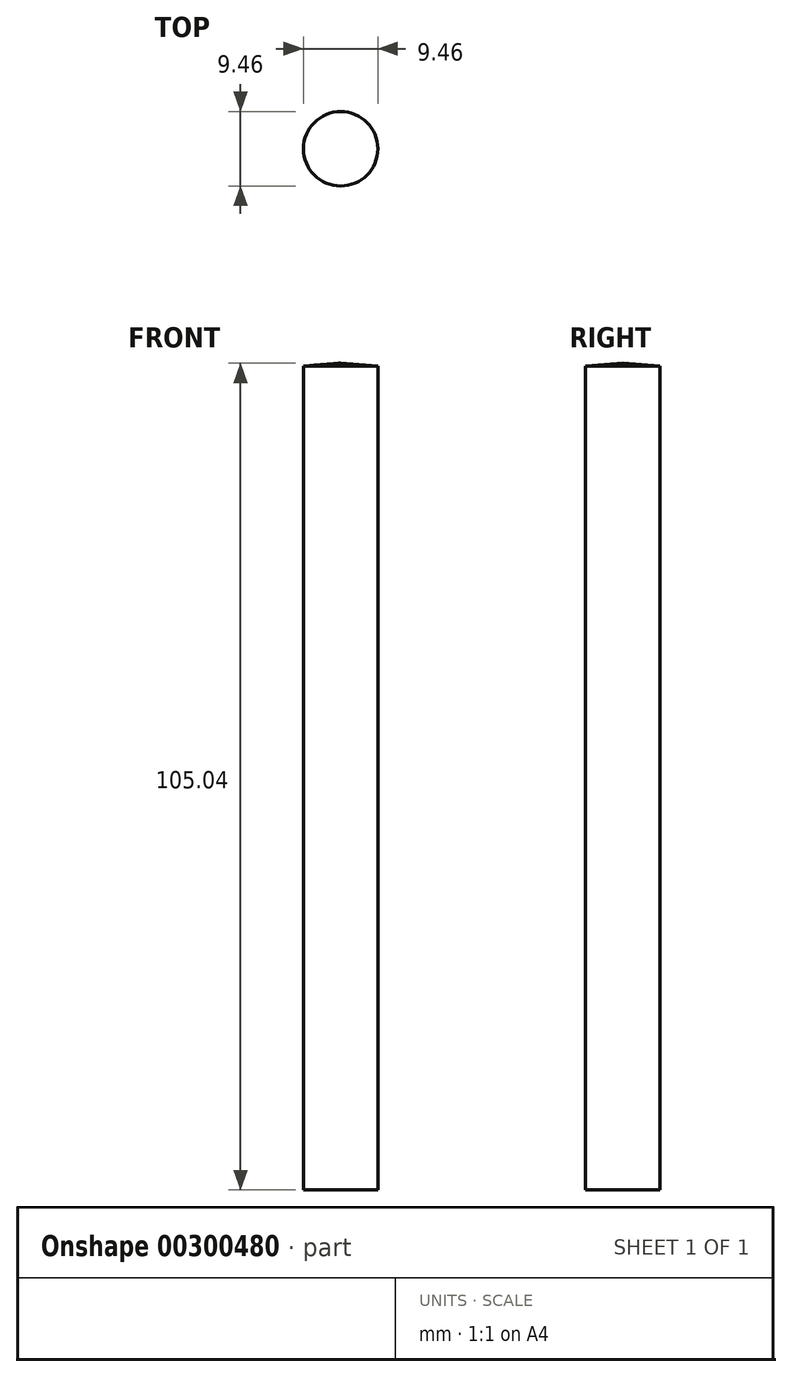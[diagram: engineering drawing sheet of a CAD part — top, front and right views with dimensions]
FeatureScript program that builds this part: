
annotation { "Feature Type Name" : "Feature", "Feature Type Description" : "" }
export const myFeature = defineFeature(function(context is Context, id is Id, definition is map)
    precondition{}
    {
        {
            var Q0;
            Q0=qCreatedBy(makeId("Front.planeOp"),FACE);
            var sketch = newSketch(context, id + "F0", { "sketchPlane" : qUnion([Q0])});
            skLineSegment(sketch, "E0", {"start": v(-44.24, 55.77) * mm, "end": v(-44.24, -49.27) * mm});
            skLineSegment(sketch, "E1", {"start": v(-44.24, -49.27) * mm, "end": v(-39.51, -49.27) * mm});
            skLineSegment(sketch, "E2", {"start": v(-39.51, -49.27) * mm, "end": v(-39.51, 55.38) * mm});
            skLineSegment(sketch, "E3", {"start": v(-39.51, 55.38) * mm, "end": v(-44.24, 55.77) * mm});
            skSolve(sketch);
        }
        {
            var Q0;
            Q0=makeQuery(id+"F0.imprint","IMPRINT",FACE,{"disambiguationData":[TD([[makeQuery(id+"F0.imprint","IMPRINT",EDGE,{"derivedFrom":sQuery(id+"F0.wireOp",EDGE,"E0")}),1.0]])]});
            var Q1;
            Q1=sQuery(id+"F0.wireOp",EDGE,"E0");
            revolve(context, id + "F1", {"entities" : qUnion([Q0]), "axis" : qUnion([Q1]), "revolveType" : RevolveType.FULL});
        }
    });
